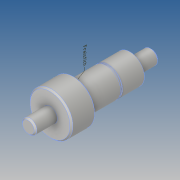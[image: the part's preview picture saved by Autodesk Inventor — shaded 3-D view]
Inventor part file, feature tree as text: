
AUTODESK INVENTOR PART (.ipt)
format: ipt  version: 2018.2 (Build 222227000, 227)  size: 140,288 bytes
history: native  units: mm
features: other x4, chamfer x2, sketch x2
ambient origin geometry x8: Origin, YZ Plane, XZ Plane, XY Plane, X Axis, Y Axis, Z Axis, Center Point
bodies: Volumenkörper1 (feature_tree)
feature tree (8):
  other  "Anmerkungen"
  other  "Grundkörper"
  other  "Nut_Sicherungsring_DIN471-20x1,2"
  chamfer  "FaseAllgemein"  Distance=22.2mm
  chamfer  "FaseLager"  Distance=55.0mm
  sketch  "Skizze1"  dims[d0=10.0mm]
  sketch  "Skizze2"  dims[d1=15.0mm d2=22.2mm d3=55.0mm d4=20.0mm d5=29.5mm d6=90.0deg d9=1.0mm d10=2.0mm d11=45.0deg d12=0.5mm d13=2.0mm d14=45.0deg d15=1.3mm d16=19.0mm d17=90.0deg d7=0.078426mm d8=0.0mm]
  other  "Führungslinientext 1"
